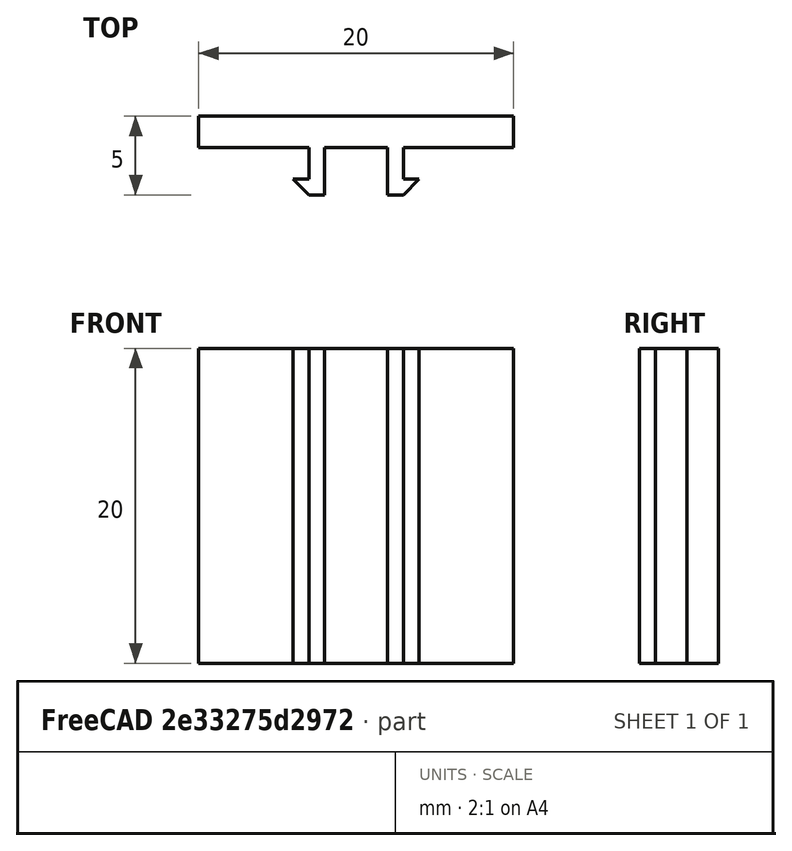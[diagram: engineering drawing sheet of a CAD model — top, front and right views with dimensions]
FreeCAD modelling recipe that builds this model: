
FCSTD DOCUMENT  (FreeCAD 0.15R4671 (Git))
Label: 2020
License: All rights reserved
LicenseURL: http://en.wikipedia.org/wiki/All_rights_reserved
objects: Sketcher::SketchObject×1, PartDesign::Pad×1
note: 3 computed .brp shape members not serialized (recipe doc carries the construction recipe); baked Part::Feature solids carry a one-line shape summary decoded from their .brp

FEATURE [Sketcher::SketchObject] Sketch
  sketch-geometry (16):
    g0: LineSegment StartX=-10 StartY=1 StartZ=0 EndX=10 EndY=1 EndZ=0
    g1: LineSegment StartX=10 StartY=1 StartZ=0 EndX=10 EndY=-1 EndZ=0
    g2: LineSegment StartX=-10 StartY=-1 StartZ=0 EndX=-10 EndY=1 EndZ=0
    g3: LineSegment StartX=-10 StartY=-1 StartZ=0 EndX=-3 EndY=-1 EndZ=0
    g4: LineSegment StartX=-3 StartY=-1 StartZ=0 EndX=-3 EndY=-3 EndZ=0
    g5: LineSegment StartX=-3 StartY=-3 StartZ=0 EndX=-4 EndY=-3 EndZ=0
    g6: LineSegment StartX=10 StartY=-1 StartZ=0 EndX=3 EndY=-1 EndZ=0
    g7: LineSegment StartX=3 StartY=-1 StartZ=0 EndX=3 EndY=-3 EndZ=0
    g8: LineSegment StartX=3 StartY=-3 StartZ=0 EndX=4 EndY=-3 EndZ=0
    g9: LineSegment StartX=-4 StartY=-3 StartZ=0 EndX=-3 EndY=-4 EndZ=0
    g10: LineSegment StartX=-3 StartY=-4 StartZ=0 EndX=-2 EndY=-4 EndZ=0
    g11: LineSegment StartX=-2 StartY=-4 StartZ=0 EndX=-2 EndY=-1 EndZ=0
    g12: LineSegment StartX=-2 StartY=-1 StartZ=0 EndX=2 EndY=-1 EndZ=0
    g13: LineSegment StartX=2 StartY=-1 StartZ=0 EndX=2 EndY=-4 EndZ=0
    g14: LineSegment StartX=2 StartY=-4 StartZ=0 EndX=3 EndY=-4 EndZ=0
    g15: LineSegment StartX=3 StartY=-4 StartZ=0 EndX=4 EndY=-3 EndZ=0
  constraints (47):
    c: Coincident(g0,g1)
    c: Coincident(g2,g0)
    c: Horizontal(g0)
    c: Vertical(g1)
    c: Vertical(g2)
    c: Symmetric(g0,g0,g-2)
    c: Symmetric(g0,g1,g-1)
    c: DistanceX(g0) = 20
    c: DistanceY(g1) = -2
    c: Coincident(g2,g3)
    c: Coincident(g3,g4)
    c: Coincident(g4,g5)
    c: Horizontal(g5)
    c: Coincident(g1,g6)
    c: Coincident(g6,g7)
    c: Vertical(g7)
    c: Coincident(g7,g8)
    c: Horizontal(g8)
    c: Horizontal(g3)
    c: Horizontal(g6)
    c: Vertical(g4)
    c: Symmetric(g3,g6,g-2)
    c: DistanceX(g3,g6) = 6
    c: Equal(g7,g4)
    c: DistanceY(g7) = -2
    c: Symmetric(g5,g8,g-2)
    c: Coincident(g5,g9)
    c: Coincident(g9,g10)
    c: Horizontal(g10)
    c: Coincident(g10,g11)
    c: Vertical(g11)
    c: Coincident(g11,g12)
    c: Horizontal(g12)
    c: Coincident(g12,g13)
    c: Vertical(g13)
    c: Coincident(g13,g14)
    c: Horizontal(g14)
    c: Coincident(g14,g15)
    c: Coincident(g15,g8)
    c: DistanceX(g11,g12) = 4
    c: Symmetric(g10,g13,g-2)
    c: DistanceY(g13) = -3
    c: Symmetric(g9,g14,g-2)
    c: Equal(g14,g10)
    c: DistanceX(g14) = 1
    c: Angle(g9,g5) = 0.785398
    c: DistanceX(g5) = -1
FEATURE [PartDesign::Pad] Pad
  Length = 20
  Length2 = 100
  Sketch = -> Sketch
  Type = 0
